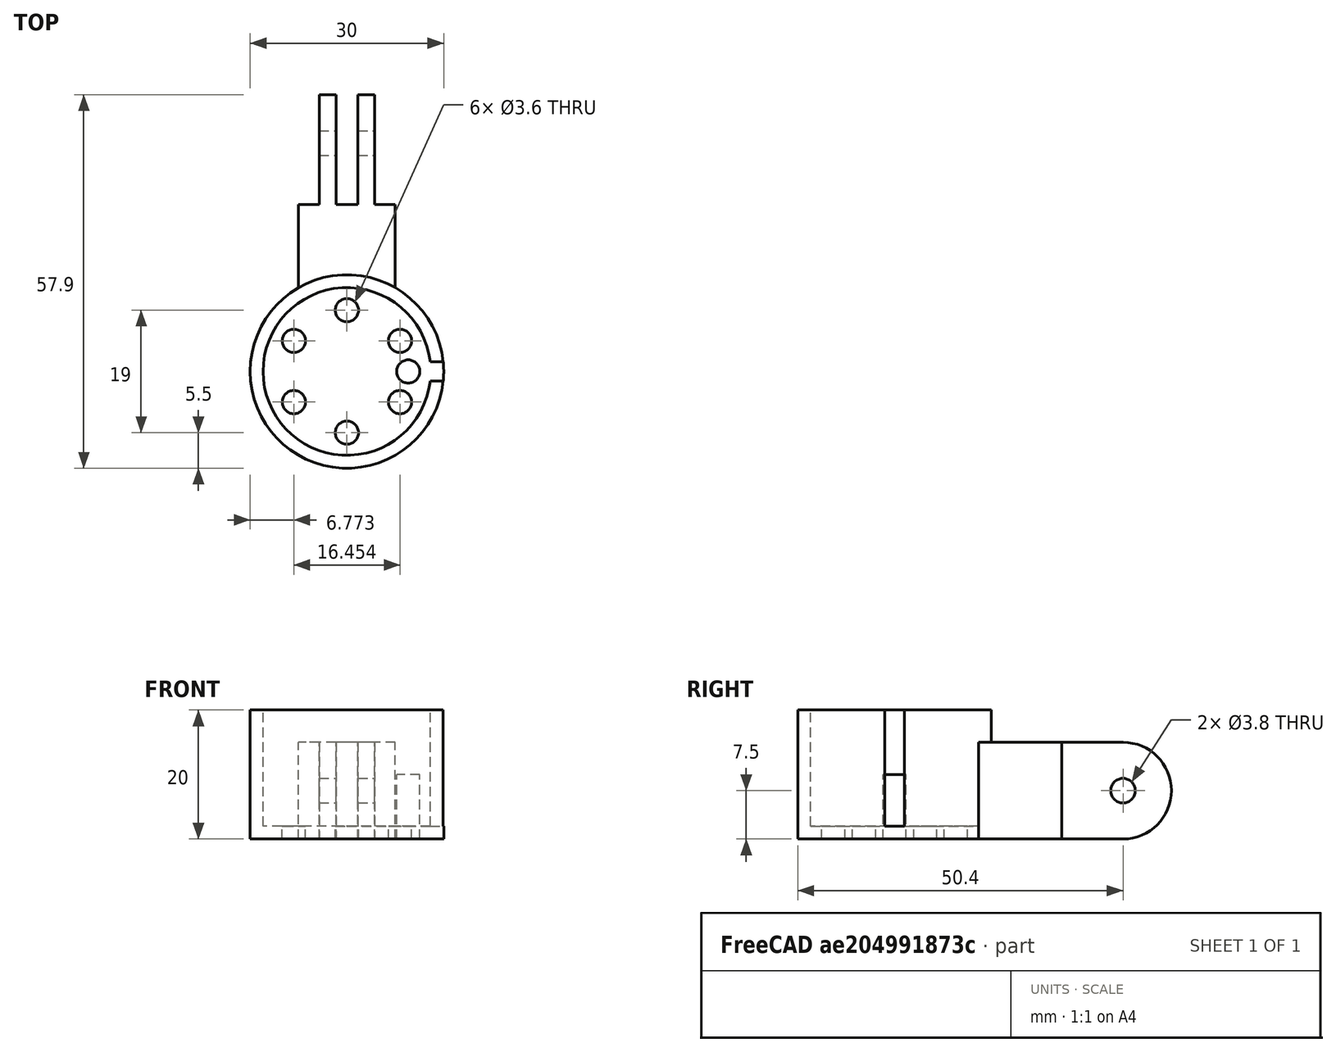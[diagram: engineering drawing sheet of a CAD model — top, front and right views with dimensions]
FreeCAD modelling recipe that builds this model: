
FCSTD DOCUMENT  (FreeCAD 0.19R23578 (Git))
Label: uv_led_container
License: All rights reserved
LicenseURL: http://en.wikipedia.org/wiki/All_rights_reserved
objects: Part::Cylinder×3, Part::MultiFuse×3, Part::Box×2, Spreadsheet::Sheet×1, Part::FeaturePython×1, Part::Feature×1, Part::Cut×1
note: 10 computed .brp shape members not serialized (recipe doc carries the construction recipe); baked Part::Feature solids carry a one-line shape summary decoded from their .brp

FEATURE [Spreadsheet::Sheet] Spreadsheet  label="p"
  cells = A1=led_hole_r; B1(led_hole_r)=13; A2=bolt_hole_r; B2(bolt_hole_r)=1.8; A3=hole_dist; B3(hole_dist)=19; A4=back_wall; B4(back_wall)=2; A5=shell_wall; B5(shell_wall)=2; A6=shell_length; B6(shell_length)=20; A7=wire_cut_size; B7(wire_cut_size)=3; A8=stick_x; B8(stick_x)=15; A9=stick_y; B9(stick_y)=15; A10=stick_length; B10(stick_length)=10
FEATURE [Part::Cylinder] Cylinder  label="outer shell"
  Angle = 360
  AttacherType = Attacher::AttachEngine3D
  Height = 20
  Radius = 15
  expr: Height = <<p>>.shell_length
  expr: Radius = <<p>>.led_hole_r + <<p>>.shell_wall
FEATURE [Part::Cylinder] Cylinder001  label="inner hole"
  Angle = 360
  AttacherType = Attacher::AttachEngine3D
  Height = 20
  Placement = pos=(0,0,2) rot=(0,0,1;0rad)
  Radius = 13
  expr: Height = <<p>>.shell_length
  expr: .Placement.Base.z = <<p>>.back_wall
  expr: Radius = Spreadsheet.led_hole_r
FEATURE [Part::Cylinder] Cylinder002  label="bolt hole"
  Angle = 360
  AttacherType = Attacher::AttachEngine3D
  Height = 10
  Placement = pos=(9.5,0,0) rot=(0,0,1;0rad)
  Radius = 1.8
  expr: .Placement.Base.x = <<p>>.hole_dist / 2
  expr: Radius = <<p>>.bolt_hole_r
FEATURE [Part::FeaturePython] Array  label="bolt hole array"  # Draft array (typed FeaturePython)
  Angle = 360
  ArrayType = 1
  Axis = (0,0,1)
  Base = -> Cylinder002
  Center = (0,0,0)
  Count = 6
  ExpandArray = false
  Fuse = false
  IntervalAxis = (0,0,0)
  IntervalX = (100,0,0)
  IntervalY = (0,100,0)
  IntervalZ = (0,0,100)
  NumberCircles = 3
  NumberPolar = 6
  NumberX = 2
  NumberY = 2
  NumberZ = 1
  Placement = pos=(0,0,0) rot=(0,0,1;0.523599rad)
  PlacementList = 6 placements: [(9.5,0,0),(4.75,8.22724,0),(-4.75,8.22724,0),(-9.5,1.16341e-15,0),(-4.75,-8.22724,0),(4.75,-8.22724,0)]
  RadialDistance = 50
  ScaleList = (6) [(1,1,1),(1,1,1),(1,1,1),(1,1,1),(1,1,1),(1,1,1)]
  Symmetry = 1
  TangentialDistance = 25
  expr: .Placement.Rotation.Angle = 360 / 6 / 2
FEATURE [Part::Box] Box  label="wire passage cube"
  AttacherType = Attacher::AttachEngine3D
  Height = 20
  Length = 15
  Placement = pos=(0,-1.5,2) rot=(0,0,1;0rad)
  Width = 3
  expr: Height = <<p>>.shell_length
  expr: Length = <<p>>.shell_wall + <<p>>.led_hole_r
  expr: .Placement.Base.y = -<<p>>.wire_cut_size / 2
  expr: Width = <<p>>.wire_cut_size
  expr: .Placement.Base.z = <<p>>.back_wall
FEATURE [Part::MultiFuse] Fusion  label="extraction fusion"
  Shapes = -> [Cylinder001,Array,Box]
FEATURE [Part::Box] Box002  label="stick cube"
  AttacherType = Attacher::AttachEngine3D
  Height = 10
  Length = 15
  Width = 15
  expr: Length = <<p>>.stick_x
  expr: Width = <<p>>.stick_y
  expr: Height = <<p>>.stick_length
FEATURE [Part::Feature] Cut001001  label="side 2 cut001"
  Placement = pos=(7.5,7.5,10) rot=(0,0,1;1.5708rad)
  shape: bbox 15 x 15 x 20 mm, 16 faces (baked)
  expr: .Placement.Base.y = <<p>>.stick_y / 2
  expr: .Placement.Base.x = <<p>>.stick_x / 2
  expr: .Placement.Base.z = <<p>>.stick_length
FEATURE [Part::MultiFuse] Fusion001  label="holder fusion"
  Placement = pos=(-7.5,12.9,15) rot=(1,0,0;4.71239rad)
  Shapes = -> [Cut001001,Box002]
FEATURE [Part::MultiFuse] Fusion002  label="body fusion"
  Shapes = -> [Cylinder,Fusion001]
FEATURE [Part::Cut] Cut  label="uv led body cut"
  Base = -> Fusion002
  Tool = -> Fusion
